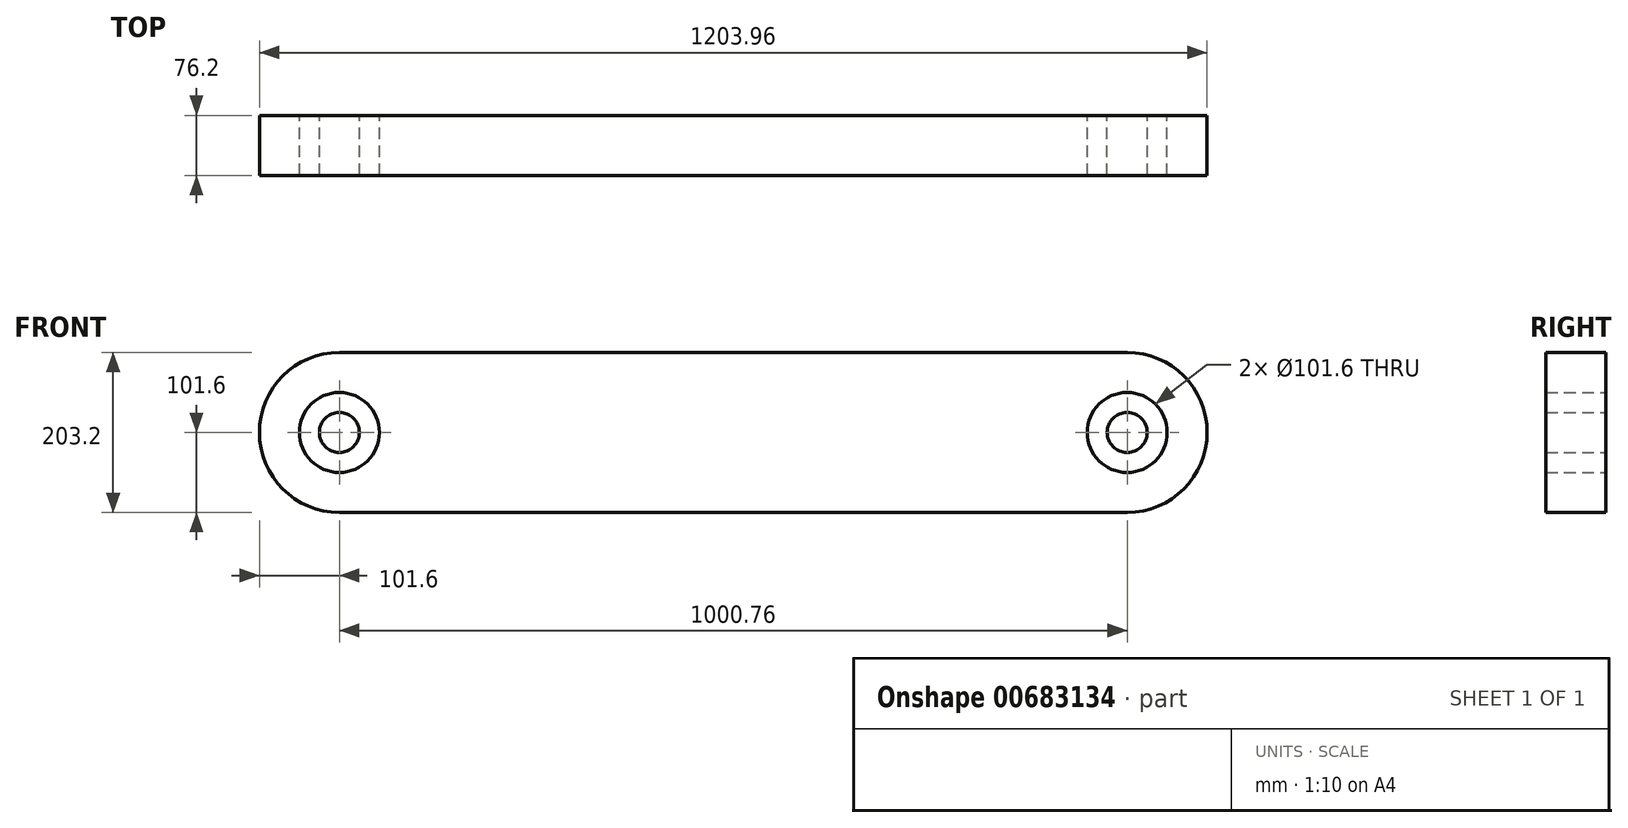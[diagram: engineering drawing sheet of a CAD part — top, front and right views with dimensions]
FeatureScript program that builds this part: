
annotation { "Feature Type Name" : "Feature", "Feature Type Description" : "" }
export const myFeature = defineFeature(function(context is Context, id is Id, definition is map)
    precondition{}
    {
        {
            var Q0;
            Q0=qCreatedBy(makeId("Front.planeOp"),FACE);
            var sketch = newSketch(context, id + "F0", { "sketchPlane" : qUnion([Q0])});
            skArc(sketch, "E0", {"start": v(0, 101.6) * mm, "mid": v(-101.6, 0) * mm, "end": v(0, -101.6) * mm});
            skArc(sketch, "E1", {"start": v(1000.76, -101.6) * mm, "mid": v(1102.36, 0) * mm, "end": v(1000.76, 101.6) * mm});
            skLineSegment(sketch, "E2", {"start": v(0, 101.6) * mm, "end": v(1000.76, 101.6) * mm});
            skLineSegment(sketch, "E3", {"start": v(0, -101.6) * mm, "end": v(1000.76, -101.6) * mm});
            skCircle(sketch, "E4", {"center": v(0, 0) * mm, "radius": 50.8 * mm});
            skCircle(sketch, "E5", {"center": v(1000.76, 0) * mm, "radius": 50.8 * mm});
            skCircle(sketch, "E6", {"center": v(0, 0) * mm, "radius": 25.4 * mm});
            skCircle(sketch, "E7", {"center": v(1000.76, 0) * mm, "radius": 25.4 * mm});
            skSolve(sketch);
        }
        {
            var Q0;
            Q0 = qSketchRegion(id + "F0", true);
            var Q1;
            Q1=makeQuery(id+"F0.imprint","IMPRINT",FACE,{"disambiguationData":[TD([[makeQuery(id+"F0.imprint","IMPRINT",EDGE,{"derivedFrom":sQuery(id+"F0.wireOp",EDGE,"E6")}),1.0]])]});
            var Q2;
            Q2=makeQuery(id+"F0.imprint","IMPRINT",FACE,{"disambiguationData":[TD([[makeQuery(id+"F0.imprint","IMPRINT",EDGE,{"derivedFrom":sQuery(id+"F0.wireOp",EDGE,"E7")}),1.0]])]});
            extrude(context, id + "F1", {"entities" : qUnion([Q0, Q1, Q2]), "depth" : 76.2 * mm, "offsetDistance" : 25.4 * mm});
        }
    });
